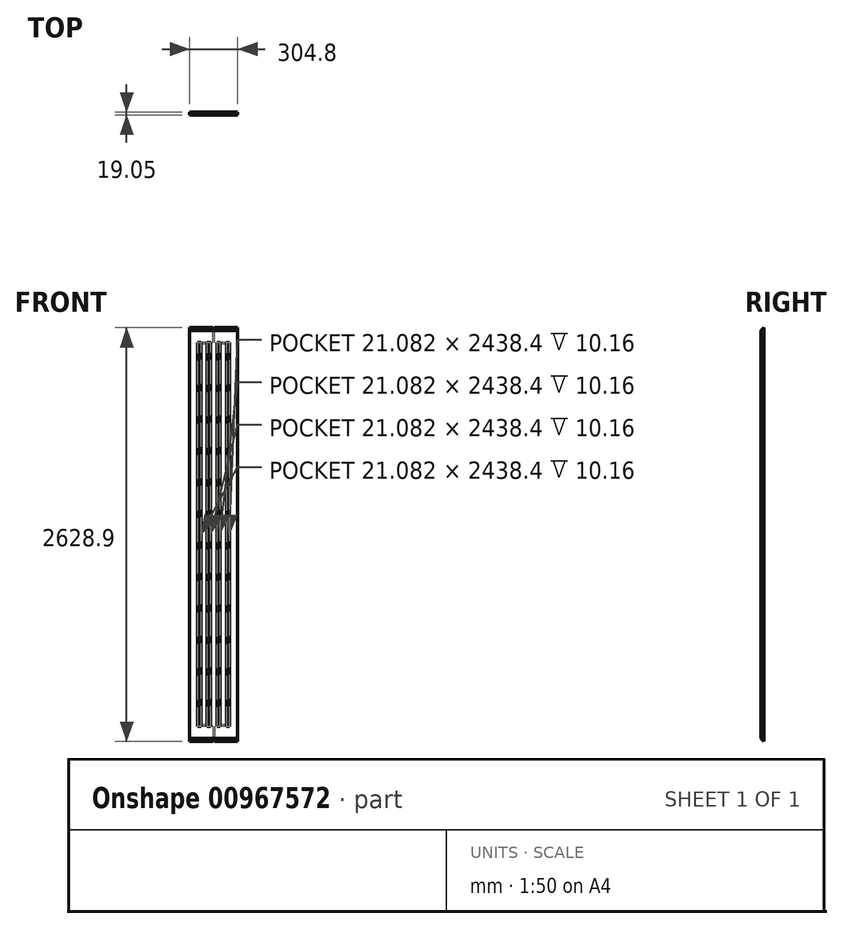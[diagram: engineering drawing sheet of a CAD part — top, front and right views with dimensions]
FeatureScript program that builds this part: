
annotation { "Feature Type Name" : "Feature", "Feature Type Description" : "" }
export const myFeature = defineFeature(function(context is Context, id is Id, definition is map)
    precondition{}
    {
        {
            var Q0;
            Q0=qCreatedBy(makeId("Front.planeOp"),FACE);
            var sketch = newSketch(context, id + "F0", { "sketchPlane" : qUnion([Q0])});
            skLineSegment(sketch, "E0.bottom", {"start": v(-155.25, 2501.37) * mm, "end": v(149.55, 2501.37) * mm});
            skLineSegment(sketch, "E0.top", {"start": v(-155.25, -127.53) * mm, "end": v(149.55, -127.53) * mm});
            skLineSegment(sketch, "E0.left", {"start": v(-155.25, 2501.37) * mm, "end": v(-155.25, -127.53) * mm});
            skLineSegment(sketch, "E0.right", {"start": v(149.55, 2501.37) * mm, "end": v(149.55, -127.53) * mm});
            skSolve(sketch);
        }
        {
            var Q0;
            Q0=makeQuery(id+"F0.imprint","IMPRINT",FACE,{"disambiguationData":[TD([[makeQuery(id+"F0.imprint","IMPRINT",EDGE,{"derivedFrom":sQuery(id+"F0.wireOp",EDGE,"E0.bottom")}),-1.0]])]});
            extrude(context, id + "F1", {"entities" : qUnion([Q0]), "depth" : 19.05 * mm, "offsetDistance" : 25.4 * mm});
        }
        {
            var Q0;
            Q0=makeQuery(id+"F1.opExtrude","CAP_EDGE",EDGE,{"disambiguationData":[OSD([sQuery(id+"F0.wireOp",EDGE,"E0.bottom")])],"isStart":false});
            var Q1;
            Q1=makeQuery(id+"F1.opExtrude","CAP_EDGE",EDGE,{"disambiguationData":[OSD([sQuery(id+"F0.wireOp",EDGE,"E0.top")])],"isStart":false});
            chamfer(context, id + "F2", {"entities" : qUnion([Q0, Q1]), "width" : 19.05 * mm});
        }
        {
            var Q0;
            Q0=makeQuery(id+"F1.opExtrude","CAP_FACE",FACE,{"disambiguationData":[OSD([sQuery(id+"F0.wireOp",EDGE,"E0.bottom"),sQuery(id+"F0.wireOp",EDGE,"E0.top"),sQuery(id+"F0.wireOp",EDGE,"E0.left"),sQuery(id+"F0.wireOp",EDGE,"E0.right")])],"isStart":false});
            var sketch = newSketch(context, id + "F3", { "sketchPlane" : qUnion([Q0])});
            skLineSegment(sketch, "E1", {"start": v(-94.3, 2482.32) * mm, "end": v(-94.3, -108.48) * mm, "construction": true});
            skLineSegment(sketch, "E2", {"start": v(-33.33, 2482.32) * mm, "end": v(-33.33, -108.48) * mm, "construction": true});
            skLineSegment(sketch, "E3.bottom", {"start": v(-104.83, 2406.12) * mm, "end": v(-83.75, 2406.12) * mm});
            skLineSegment(sketch, "E3.top", {"start": v(-104.83, -32.28) * mm, "end": v(-83.75, -32.28) * mm});
            skLineSegment(sketch, "E3.left", {"start": v(-104.83, 2406.12) * mm, "end": v(-104.83, -32.28) * mm});
            skLineSegment(sketch, "E3.right", {"start": v(-83.75, 2406.12) * mm, "end": v(-83.75, -32.28) * mm});
            skLineSegment(sketch, "E4.bottom", {"start": v(-22.8, -32.28) * mm, "end": v(-43.87, -32.28) * mm});
            skLineSegment(sketch, "E4.top", {"start": v(-22.8, 2406.12) * mm, "end": v(-43.87, 2406.12) * mm});
            skLineSegment(sketch, "E4.left", {"start": v(-22.8, -32.28) * mm, "end": v(-22.8, 2406.12) * mm});
            skLineSegment(sketch, "E4.right", {"start": v(-43.87, -32.28) * mm, "end": v(-43.87, 2406.12) * mm});
            skLineSegment(sketch, "E5", {"start": v(27.63, 2482.32) * mm, "end": v(27.63, -108.48) * mm, "construction": true});
            skLineSegment(sketch, "E6.bottom", {"start": v(17.09, 2406.12) * mm, "end": v(38.17, 2406.12) * mm});
            skLineSegment(sketch, "E6.top", {"start": v(17.09, -32.28) * mm, "end": v(38.17, -32.28) * mm});
            skLineSegment(sketch, "E6.left", {"start": v(17.09, 2406.12) * mm, "end": v(17.09, -32.28) * mm});
            skLineSegment(sketch, "E6.right", {"start": v(38.17, 2406.12) * mm, "end": v(38.17, -32.28) * mm});
            skLineSegment(sketch, "E7", {"start": v(88.59, -108.48) * mm, "end": v(88.59, 2482.32) * mm, "construction": true});
            skLineSegment(sketch, "E8.bottom", {"start": v(99.13, -32.28) * mm, "end": v(78.05, -32.28) * mm});
            skLineSegment(sketch, "E8.top", {"start": v(99.13, 2406.12) * mm, "end": v(78.05, 2406.12) * mm});
            skLineSegment(sketch, "E8.left", {"start": v(99.13, -32.28) * mm, "end": v(99.13, 2406.12) * mm});
            skLineSegment(sketch, "E8.right", {"start": v(78.05, -32.28) * mm, "end": v(78.05, 2406.12) * mm});
            skSolve(sketch);
        }
        {
            var Q0;
            Q0=makeQuery(id+"F3.imprint","IMPRINT",FACE,{"disambiguationData":[TD([[makeQuery(id+"F3.imprint","IMPRINT",EDGE,{"derivedFrom":sQuery(id+"F3.wireOp",EDGE,"E3.bottom")}),-1.0]])]});
            var Q1;
            Q1=makeQuery(id+"F3.imprint","IMPRINT",FACE,{"disambiguationData":[TD([[makeQuery(id+"F3.imprint","IMPRINT",EDGE,{"derivedFrom":sQuery(id+"F3.wireOp",EDGE,"E4.bottom")}),-1.0]])]});
            var Q2;
            Q2=makeQuery(id+"F3.imprint","IMPRINT",FACE,{"disambiguationData":[TD([[makeQuery(id+"F3.imprint","IMPRINT",EDGE,{"derivedFrom":sQuery(id+"F3.wireOp",EDGE,"E6.bottom")}),-1.0]])]});
            var Q3;
            Q3=makeQuery(id+"F3.imprint","IMPRINT",FACE,{"disambiguationData":[TD([[makeQuery(id+"F3.imprint","IMPRINT",EDGE,{"derivedFrom":sQuery(id+"F3.wireOp",EDGE,"E8.bottom")}),-1.0]])]});
            extrude(context, id + "F4", {"entities" : qUnion([Q0, Q1, Q2, Q3]), "operationType" : NewBodyOperationType.REMOVE, "oppositeDirection" : true, "depth" : 10.16 * mm, "offsetDistance" : 25.4 * mm});
        }
        {
            var Q0;
            Q0=makeQuery(id+"F1.opExtrude","CAP_FACE",FACE,{"disambiguationData":[OSD([sQuery(id+"F0.wireOp",EDGE,"E0.bottom"),sQuery(id+"F0.wireOp",EDGE,"E0.top"),sQuery(id+"F0.wireOp",EDGE,"E0.left"),sQuery(id+"F0.wireOp",EDGE,"E0.right")])],"isStart":true});
            var sketch = newSketch(context, id + "F5", { "sketchPlane" : qUnion([Q0])});
            skLineSegment(sketch, "E9.bottom", {"start": v(-99.13, 2406.12) * mm, "end": v(-1.9, 2406.12) * mm});
            skLineSegment(sketch, "E9.top", {"start": v(-99.13, 2396.6) * mm, "end": v(104.83, 2396.6) * mm});
            skLineSegment(sketch, "E9.left", {"start": v(-99.13, 2406.12) * mm, "end": v(-99.13, 2396.6) * mm});
            skLineSegment(sketch, "E9.right", {"start": v(104.83, 2406.12) * mm, "end": v(104.83, 2396.6) * mm});
            skLineSegment(sketch, "E10.bottom", {"start": v(-1.9, 2406.12) * mm, "end": v(7.62, 2406.12) * mm});
            skLineSegment(sketch, "E10.top", {"start": v(-1.9, 2501.37) * mm, "end": v(7.62, 2501.37) * mm});
            skLineSegment(sketch, "E10.left", {"start": v(-1.9, 2406.12) * mm, "end": v(-1.9, 2501.37) * mm});
            skLineSegment(sketch, "E10.right", {"start": v(7.62, 2406.12) * mm, "end": v(7.62, 2501.37) * mm});
            skLineSegment(sketch, "E11", {"start": v(2.85, 2535.27) * mm, "end": v(2.85, 2297.66) * mm, "construction": true});
            skLineSegment(sketch, "E12.trimOffspring", {"start": v(7.62, 2406.12) * mm, "end": v(104.83, 2406.12) * mm});
            skLineSegment(sketch, "E13", {"start": v(-390.9, 1186.92) * mm, "end": v(413, 1186.92) * mm, "construction": true});
            skLineSegment(sketch, "E14.MirrorCS", {"start": v(-1.9, -32.28) * mm, "end": v(7.62, -32.28) * mm});
            skLineSegment(sketch, "E15.MirrorCS", {"start": v(-1.9, -127.53) * mm, "end": v(7.62, -127.53) * mm});
            skLineSegment(sketch, "E16.MirrorCS", {"start": v(-99.13, -32.28) * mm, "end": v(-99.13, -22.75) * mm});
            skLineSegment(sketch, "E17.MirrorCS", {"start": v(104.83, -32.28) * mm, "end": v(104.83, -22.75) * mm});
            skLineSegment(sketch, "E18.MirrorCS", {"start": v(7.62, -32.28) * mm, "end": v(7.62, -127.53) * mm});
            skLineSegment(sketch, "E19.MirrorCS", {"start": v(-1.9, -32.28) * mm, "end": v(-1.9, -127.53) * mm});
            skLineSegment(sketch, "E20.MirrorCS", {"start": v(-99.13, -32.28) * mm, "end": v(-1.9, -32.28) * mm});
            skLineSegment(sketch, "E21.MirrorCS", {"start": v(2.85, -161.42) * mm, "end": v(2.85, 76.18) * mm, "construction": true});
            skLineSegment(sketch, "E22.MirrorCS", {"start": v(-99.13, -22.75) * mm, "end": v(104.83, -22.75) * mm});
            skLineSegment(sketch, "E23.MirrorCS", {"start": v(7.62, -32.28) * mm, "end": v(104.83, -32.28) * mm});
            skSolve(sketch);
        }
        {
            var Q0;
            Q0=makeQuery(id+"F5.imprint","IMPRINT",FACE,{"disambiguationData":[TD([[makeQuery(id+"F5.imprint","IMPRINT",EDGE,{"derivedFrom":sQuery(id+"F5.wireOp",EDGE,"E9.bottom")}),-1.0]])]});
            var Q1;
            Q1=makeQuery(id+"F5.imprint","IMPRINT",FACE,{"disambiguationData":[TD([[makeQuery(id+"F5.imprint","IMPRINT",EDGE,{"derivedFrom":sQuery(id+"F5.wireOp",EDGE,"E10.bottom")}),1.0]])]});
            var Q2;
            Q2=makeQuery(id+"F5.imprint","IMPRINT",FACE,{"disambiguationData":[TD([[makeQuery(id+"F5.imprint","IMPRINT",EDGE,{"derivedFrom":sQuery(id+"F5.wireOp",EDGE,"E14.MirrorCS")}),-1.0]])]});
            var Q3;
            Q3=makeQuery(id+"F5.imprint","IMPRINT",FACE,{"disambiguationData":[TD([[makeQuery(id+"F5.imprint","IMPRINT",EDGE,{"derivedFrom":sQuery(id+"F5.wireOp",EDGE,"E14.MirrorCS")}),1.0]])]});
            extrude(context, id + "F6", {"entities" : qUnion([Q0, Q1, Q2, Q3]), "operationType" : NewBodyOperationType.REMOVE, "oppositeDirection" : true, "depth" : 6.35 * mm, "offsetDistance" : 25.4 * mm});
        }
    });
